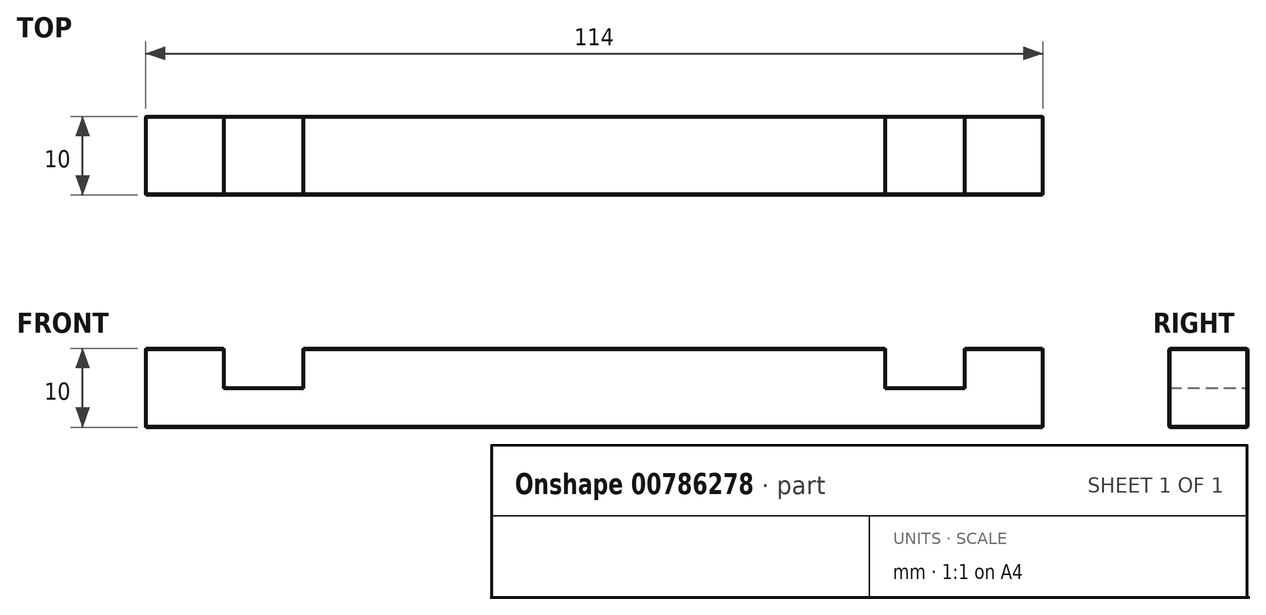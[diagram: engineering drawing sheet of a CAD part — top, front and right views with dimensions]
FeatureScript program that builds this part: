
annotation { "Feature Type Name" : "Feature", "Feature Type Description" : "" }
export const myFeature = defineFeature(function(context is Context, id is Id, definition is map)
    precondition{}
    {
        {
            var Q0;
            Q0=qCreatedBy(makeId("Front.planeOp"),FACE);
            var sketch = newSketch(context, id + "F0", { "sketchPlane" : qUnion([Q0])});
            skLineSegment(sketch, "E0", {"start": v(-46.64, 10) * mm, "end": v(-46.64, 0) * mm});
            skLineSegment(sketch, "E1", {"start": v(-46.64, 0) * mm, "end": v(67.36, 0) * mm});
            skLineSegment(sketch, "E2", {"start": v(67.36, 0) * mm, "end": v(67.36, 10) * mm});
            skLineSegment(sketch, "E3", {"start": v(67.36, 10) * mm, "end": v(57.36, 10) * mm});
            skLineSegment(sketch, "E4", {"start": v(57.36, 10) * mm, "end": v(57.36, 5) * mm});
            skLineSegment(sketch, "E5", {"start": v(57.36, 5) * mm, "end": v(47.36, 5) * mm});
            skLineSegment(sketch, "E6", {"start": v(47.36, 5) * mm, "end": v(47.36, 10) * mm});
            skLineSegment(sketch, "E7", {"start": v(47.36, 10) * mm, "end": v(-26.64, 10) * mm});
            skLineSegment(sketch, "E8", {"start": v(-26.64, 10) * mm, "end": v(-26.64, 5) * mm});
            skLineSegment(sketch, "E9", {"start": v(-26.64, 5) * mm, "end": v(-36.64, 5) * mm});
            skLineSegment(sketch, "E10", {"start": v(-36.64, 5) * mm, "end": v(-36.64, 10) * mm});
            skLineSegment(sketch, "E11", {"start": v(-36.64, 10) * mm, "end": v(-46.64, 10) * mm});
            skSolve(sketch);
        }
        {
            var Q0;
            Q0 = qSketchRegion(id + "F0", true);
            extrude(context, id + "F1", {"entities" : qUnion([Q0]), "depth" : 10 * mm, "offsetDistance" : 25 * mm});
        }
        {
            var Q0;
            Q0=makeQuery(id+"F1.opExtrude","CAP_EDGE",EDGE,{"disambiguationData":[OSD([sQuery(id+"F0.wireOp",EDGE,"E7")])],"isStart":false});
            var Q1;
            Q1=makeQuery(id+"F1.opExtrude","CAP_EDGE",EDGE,{"disambiguationData":[OSD([sQuery(id+"F0.wireOp",EDGE,"E7")])],"isStart":true});
            var Q2;
            Q2=makeQuery(id+"F1.opExtrude","SWEPT_EDGE",EDGE,{"disambiguationData":[OSD([sQuery(id+"F0.wireOp",EDGE,"E6"),sQuery(id+"F0.wireOp",EDGE,"E7")])]});
            var Q3;
            Q3=makeQuery(id+"F1.opExtrude","CAP_EDGE",EDGE,{"disambiguationData":[OSD([sQuery(id+"F0.wireOp",EDGE,"E6")])],"isStart":false});
            var Q4;
            Q4=makeQuery(id+"F1.opExtrude","CAP_EDGE",EDGE,{"disambiguationData":[OSD([sQuery(id+"F0.wireOp",EDGE,"E6")])],"isStart":true});
            var Q5;
            Q5=makeQuery(id+"F1.opExtrude","SWEPT_EDGE",EDGE,{"disambiguationData":[OSD([sQuery(id+"F0.wireOp",EDGE,"E3"),sQuery(id+"F0.wireOp",EDGE,"E4")])]});
            var Q6;
            Q6=makeQuery(id+"F1.opExtrude","CAP_EDGE",EDGE,{"disambiguationData":[OSD([sQuery(id+"F0.wireOp",EDGE,"E4")])],"isStart":false});
            var Q7;
            Q7=makeQuery(id+"F1.opExtrude","CAP_FACE",FACE,{"disambiguationData":[OSD([sQuery(id+"F0.wireOp",EDGE,"E0"),sQuery(id+"F0.wireOp",EDGE,"E1"),sQuery(id+"F0.wireOp",EDGE,"E2"),sQuery(id+"F0.wireOp",EDGE,"E3"),sQuery(id+"F0.wireOp",EDGE,"E4"),sQuery(id+"F0.wireOp",EDGE,"E5"),sQuery(id+"F0.wireOp",EDGE,"E6"),sQuery(id+"F0.wireOp",EDGE,"E7"),sQuery(id+"F0.wireOp",EDGE,"E8"),sQuery(id+"F0.wireOp",EDGE,"E9"),sQuery(id+"F0.wireOp",EDGE,"E10"),sQuery(id+"F0.wireOp",EDGE,"E11")])],"isStart":false});
            var Q8;
            Q8=makeQuery(id+"F1.opExtrude","SWEPT_FACE",FACE,{"disambiguationData":[OSD([sQuery(id+"F0.wireOp",EDGE,"E3")])]});
            var Q9;
            Q9=makeQuery(id+"F1.opExtrude","SWEPT_FACE",FACE,{"disambiguationData":[OSD([sQuery(id+"F0.wireOp",EDGE,"E2")])]});
            var Q10;
            Q10=makeQuery(id+"F1.opExtrude","SWEPT_FACE",FACE,{"disambiguationData":[OSD([sQuery(id+"F0.wireOp",EDGE,"E11")])]});
            var Q11;
            Q11=makeQuery(id+"F1.opExtrude","SWEPT_FACE",FACE,{"disambiguationData":[OSD([sQuery(id+"F0.wireOp",EDGE,"E0")])]});
            var Q12;
            Q12=makeQuery(id+"F1.opExtrude","CAP_FACE",FACE,{"disambiguationData":[OSD([sQuery(id+"F0.wireOp",EDGE,"E0"),sQuery(id+"F0.wireOp",EDGE,"E1"),sQuery(id+"F0.wireOp",EDGE,"E2"),sQuery(id+"F0.wireOp",EDGE,"E3"),sQuery(id+"F0.wireOp",EDGE,"E4"),sQuery(id+"F0.wireOp",EDGE,"E5"),sQuery(id+"F0.wireOp",EDGE,"E6"),sQuery(id+"F0.wireOp",EDGE,"E7"),sQuery(id+"F0.wireOp",EDGE,"E8"),sQuery(id+"F0.wireOp",EDGE,"E9"),sQuery(id+"F0.wireOp",EDGE,"E10"),sQuery(id+"F0.wireOp",EDGE,"E11")])],"isStart":true});
            var Q13;
            Q13=makeQuery(id+"F1.opExtrude","SWEPT_EDGE",EDGE,{"disambiguationData":[OSD([sQuery(id+"F0.wireOp",EDGE,"E7"),sQuery(id+"F0.wireOp",EDGE,"E8")])]});
            var Q14;
            Q14=makeQuery(id+"F1.opExtrude","SWEPT_FACE",FACE,{"disambiguationData":[OSD([sQuery(id+"F0.wireOp",EDGE,"E7")])]});
            chamfer(context, id + "F2", {"entities" : qUnion([Q0, Q1, Q2, Q3, Q4, Q5, Q6, Q7, Q8, Q9, Q10, Q11, Q12, Q13, Q14]), "width" : 0.1 * mm, "tangentPropagation" : true});
        }
    });
